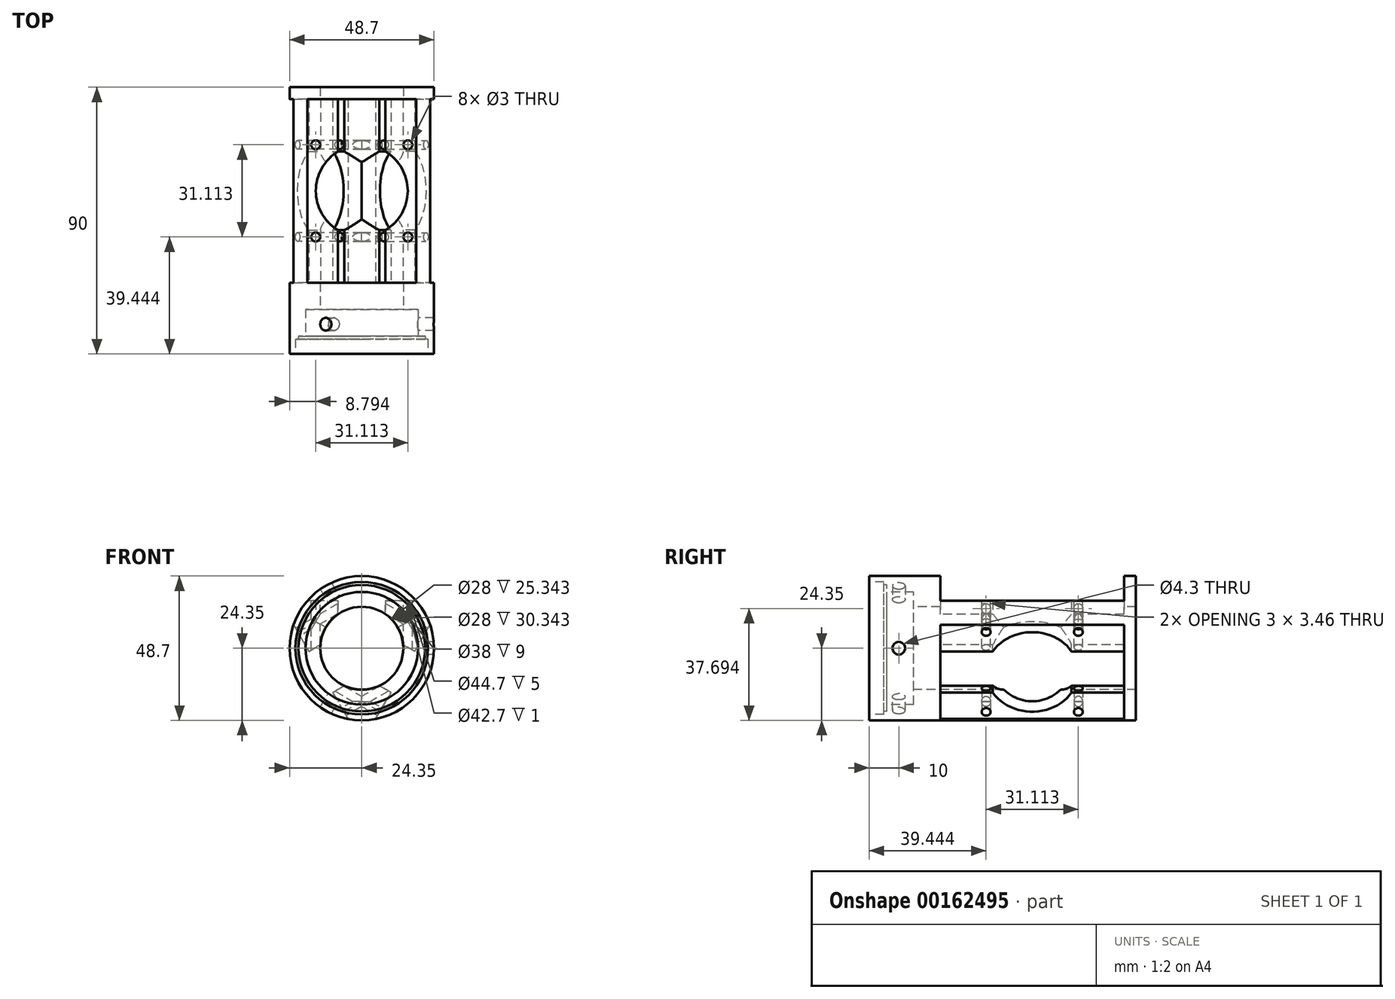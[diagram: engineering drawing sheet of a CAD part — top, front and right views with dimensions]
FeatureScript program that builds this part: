
annotation { "Feature Type Name" : "Feature", "Feature Type Description" : "" }
export const myFeature = defineFeature(function(context is Context, id is Id, definition is map)
    precondition{}
    {
        {
            var Q0;
            Q0=qCreatedBy(makeId("Top.planeOp"),FACE);
            var sketch = newSketch(context, id + "F0", { "sketchPlane" : qUnion([Q0])});
            skLineSegment(sketch, "E0", {"start": v(22.35, 0) * mm, "end": v(22.35, 5) * mm});
            skLineSegment(sketch, "E1", {"start": v(22.35, 0) * mm, "end": v(24.35, 0) * mm});
            skLineSegment(sketch, "E2", {"start": v(24.35, 0) * mm, "end": v(24.35, 90) * mm});
            skLineSegment(sketch, "E3", {"start": v(24.35, 90) * mm, "end": v(14, 90) * mm});
            skLineSegment(sketch, "E4", {"start": v(22.35, 5) * mm, "end": v(21.35, 5) * mm});
            skLineSegment(sketch, "E5", {"start": v(21.35, 5) * mm, "end": v(21.35, 6) * mm});
            skLineSegment(sketch, "E6", {"start": v(21.35, 6) * mm, "end": v(19, 6) * mm});
            skLineSegment(sketch, "E7", {"start": v(14, 90) * mm, "end": v(14, 15) * mm});
            skLineSegment(sketch, "E8", {"start": v(0, 0) * mm, "end": v(0, 47.68) * mm, "construction": true});
            skLineSegment(sketch, "E9", {"start": v(14, 15) * mm, "end": v(19, 15) * mm});
            skLineSegment(sketch, "E10", {"start": v(19, 15) * mm, "end": v(19, 6) * mm});
            skSolve(sketch);
        }
        {
            var Q0;
            Q0 = qSketchRegion(id + "F0", true);
            var Q1;
            Q1=sQuery(id+"F0.wireOp",EDGE,"E8");
            revolve(context, id + "F1", {"entities" : qUnion([Q0]), "axis" : qUnion([Q1]), "revolveType" : RevolveType.FULL});
        }
        {
            var Q0;
            Q0=qCreatedBy(makeId("Top.planeOp"),FACE);
            cPlane(context, id + "F2", {"entities" : qUnion([Q0]), "cplaneType" : CPlaneType.OFFSET, "offset" : 25 * mm, "width" : 150 * mm, "height" : 150 * mm});
        }
        {
            var Q0;
            Q0=makeQuery(id+"F1.opRevolve","SWEPT_FACE",FACE,{"disambiguationData":[OSD([sQuery(id+"F0.wireOp",EDGE,"E3")])]});
            cPlane(context, id + "F3", {"entities" : qUnion([Q0]), "cplaneType" : CPlaneType.OFFSET, "offset" : 35 * mm, "oppositeDirection" : true, "width" : 150 * mm, "height" : 150 * mm});
        }
        {
            var Q0;
            Q0=qCreatedBy(id+"F3.planeOp",FACE);
            var sketch = newSketch(context, id + "F4", { "sketchPlane" : qUnion([Q0])});
            skLineSegment(sketch, "E11.bottom", {"start": v(-30, 36) * mm, "end": v(30, 36) * mm});
            skLineSegment(sketch, "E11.top", {"start": v(-30, 16) * mm, "end": v(-8, 16) * mm});
            skLineSegment(sketch, "E11.left", {"start": v(-30, 36) * mm, "end": v(-30, 16) * mm});
            skLineSegment(sketch, "E11.right", {"start": v(30, 36) * mm, "end": v(30, 16) * mm});
            skLineSegment(sketch, "E12", {"start": v(0, 0) * mm, "end": v(0, 8.26) * mm, "construction": true});
            skLineSegment(sketch, "E13", {"start": v(-8, 16) * mm, "end": v(-8, 0) * mm});
            skLineSegment(sketch, "E14.MirrorCS", {"start": v(8, 16) * mm, "end": v(8, 0) * mm});
            skLineSegment(sketch, "E15", {"start": v(-8, 0) * mm, "end": v(8, 0) * mm});
            skLineSegment(sketch, "E16.trimOffspring", {"start": v(8, 16) * mm, "end": v(30, 16) * mm});
            skSolve(sketch);
        }
        {
            var Q0;
            Q0 = qSketchRegion(id + "F4", true);
            extrude(context, id + "F5", {"entities" : qUnion([Q0]), "endBound" : BoundingType.SYMMETRIC, "depth" : 62 * mm});
        }
        {
            var Q0;
            Q0=makeQuery(id+"F5.opExtrude","SWEPT_BODY",BODY,{"disambiguationData":[OSD([sQuery(id+"F4.wireOp",EDGE,"E11.bottom"),sQuery(id+"F4.wireOp",EDGE,"E11.top"),sQuery(id+"F4.wireOp",EDGE,"E11.left"),sQuery(id+"F4.wireOp",EDGE,"E11.right")])]});
            var Q1;
            Q1=makeQuery(id+"F1.opRevolve","SWEPT_FACE",FACE,{"disambiguationData":[OSD([sQuery(id+"F0.wireOp",EDGE,"E7")])]});
            circularPattern(context, id + "F6", {"entities" : qUnion([Q0]), "axis" : qUnion([Q1]), "angle" : 120 * degree, "instanceCount" : 3});
        }
        {
            var Q0;
            Q0=makeQuery(id+"F5.opExtrude","SWEPT_BODY",BODY,{"disambiguationData":[OSD([sQuery(id+"F4.wireOp",EDGE,"E11.bottom"),sQuery(id+"F4.wireOp",EDGE,"E11.top"),sQuery(id+"F4.wireOp",EDGE,"E11.left"),sQuery(id+"F4.wireOp",EDGE,"E11.right")])]});
            var Q1;
            Q1=makeQuery(id+"F6.opPattern","COPY",BODY,{"derivedFrom":makeQuery(id+"F5.opExtrude","SWEPT_BODY",BODY,{"disambiguationData":[OSD([sQuery(id+"F4.wireOp",EDGE,"E11.bottom"),sQuery(id+"F4.wireOp",EDGE,"E11.top"),sQuery(id+"F4.wireOp",EDGE,"E11.left"),sQuery(id+"F4.wireOp",EDGE,"E11.right")])]}),"instanceName":"2"});
            var Q2;
            Q2=makeQuery(id+"F6.opPattern","COPY",BODY,{"derivedFrom":makeQuery(id+"F5.opExtrude","SWEPT_BODY",BODY,{"disambiguationData":[OSD([sQuery(id+"F4.wireOp",EDGE,"E11.bottom"),sQuery(id+"F4.wireOp",EDGE,"E11.top"),sQuery(id+"F4.wireOp",EDGE,"E11.left"),sQuery(id+"F4.wireOp",EDGE,"E11.right")])]}),"instanceName":"1"});
            var Q3;
            Q3=makeQuery(id+"F1.opRevolve","SWEPT_BODY",BODY,{"disambiguationData":[OSD([sQuery(id+"F0.wireOp",EDGE,"E0"),sQuery(id+"F0.wireOp",EDGE,"E1"),sQuery(id+"F0.wireOp",EDGE,"E2"),sQuery(id+"F0.wireOp",EDGE,"E3"),sQuery(id+"F0.wireOp",EDGE,"E4"),sQuery(id+"F0.wireOp",EDGE,"E5"),sQuery(id+"F0.wireOp",EDGE,"E6"),sQuery(id+"F0.wireOp",EDGE,"E7")])]});
            booleanBodies(context, id + "F7", {"operationType" : BooleanOperationType.SUBTRACTION, "tools" : qUnion([Q0, Q1, Q2]), "targets" : qUnion([Q3])});
        }
        {
            var Q0;
            Q0=qCreatedBy(id+"F2.planeOp",FACE);
            var sketch = newSketch(context, id + "F8", { "sketchPlane" : qUnion([Q0])});
            skCircle(sketch, "E17", {"center": v(0, 55) * mm, "radius": 22 * mm, "construction": true});
            skLineSegment(sketch, "E18", {"start": v(0, 55) * mm, "end": v(18.83, 73.83) * mm, "construction": true});
            skCircle(sketch, "E19", {"center": v(15.56, 70.56) * mm, "radius": 1.5 * mm});
            skLineSegment(sketch, "E20", {"start": v(0, 55) * mm, "end": v(-13.28, 68.28) * mm, "construction": true});
            skCircle(sketch, "E21.MirrorC", {"center": v(-15.56, 39.44) * mm, "radius": 1.5 * mm});
            skLineSegment(sketch, "E22", {"start": v(0, 55) * mm, "end": v(-17.58, 55) * mm, "construction": true});
            skCircle(sketch, "E23.MirrorC", {"center": v(-15.56, 70.56) * mm, "radius": 1.5 * mm});
            skCircle(sketch, "E24.MirrorC", {"center": v(15.56, 39.44) * mm, "radius": 1.5 * mm});
            skSolve(sketch);
        }
        {
            var Q0;
            Q0 = qSketchRegion(id + "F8", true);
            extrude(context, id + "F9", {"entities" : qUnion([Q0]), "endBound" : BoundingType.THROUGH_ALL, "oppositeDirection" : true, "depth" : 25 * mm});
        }
        {
            var Q0;
            Q0=makeQuery(id+"F9.opExtrude","SWEPT_BODY",BODY,{"disambiguationData":[OSD([sQuery(id+"F8.wireOp",EDGE,"E19")])]});
            var Q1;
            Q1=makeQuery(id+"F9.opExtrude","SWEPT_BODY",BODY,{"disambiguationData":[OSD([sQuery(id+"F8.wireOp",EDGE,"E21.MirrorC")])]});
            var Q2;
            Q2=makeQuery(id+"F9.opExtrude","SWEPT_BODY",BODY,{"disambiguationData":[OSD([sQuery(id+"F8.wireOp",EDGE,"E24.MirrorC")])]});
            var Q3;
            Q3=makeQuery(id+"F9.opExtrude","SWEPT_BODY",BODY,{"disambiguationData":[OSD([sQuery(id+"F8.wireOp",EDGE,"E23.MirrorC")])]});
            var Q4;
            Q4=makeQuery(id+"F7.opBoolean","SPLIT",FACE,{"disambiguationData":[TD([makeQuery(id+"F1.opRevolve","SWEPT_FACE",FACE,{"disambiguationData":[OSD([sQuery(id+"F0.wireOp",EDGE,"E6")])]})])],"derivedFrom":makeQuery(id+"F1.opRevolve","SWEPT_FACE",FACE,{"disambiguationData":[OSD([sQuery(id+"F0.wireOp",EDGE,"E7")])]})});
            circularPattern(context, id + "F10", {"entities" : qUnion([Q0, Q1, Q2, Q3]), "axis" : qUnion([Q4]), "angle" : 120 * degree, "instanceCount" : 3});
        }
        {
            var Q0;
            Q0=makeQuery(id+"F9.opExtrude","SWEPT_BODY",BODY,{"disambiguationData":[OSD([sQuery(id+"F8.wireOp",EDGE,"E19")])]});
            var Q1;
            Q1=makeQuery(id+"F10.opPattern","COPY",BODY,{"derivedFrom":makeQuery(id+"F9.opExtrude","SWEPT_BODY",BODY,{"disambiguationData":[OSD([sQuery(id+"F8.wireOp",EDGE,"E21.MirrorC")])]}),"instanceName":"2"});
            var Q2;
            Q2=makeQuery(id+"F10.opPattern","COPY",BODY,{"derivedFrom":makeQuery(id+"F9.opExtrude","SWEPT_BODY",BODY,{"disambiguationData":[OSD([sQuery(id+"F8.wireOp",EDGE,"E21.MirrorC")])]}),"instanceName":"1"});
            var Q3;
            Q3=makeQuery(id+"F10.opPattern","COPY",BODY,{"derivedFrom":makeQuery(id+"F9.opExtrude","SWEPT_BODY",BODY,{"disambiguationData":[OSD([sQuery(id+"F8.wireOp",EDGE,"E19")])]}),"instanceName":"2"});
            var Q4;
            Q4=makeQuery(id+"F9.opExtrude","SWEPT_BODY",BODY,{"disambiguationData":[OSD([sQuery(id+"F8.wireOp",EDGE,"E21.MirrorC")])]});
            var Q5;
            Q5=makeQuery(id+"F10.opPattern","COPY",BODY,{"derivedFrom":makeQuery(id+"F9.opExtrude","SWEPT_BODY",BODY,{"disambiguationData":[OSD([sQuery(id+"F8.wireOp",EDGE,"E19")])]}),"instanceName":"1"});
            var Q6;
            Q6=makeQuery(id+"F9.opExtrude","SWEPT_BODY",BODY,{"disambiguationData":[OSD([sQuery(id+"F8.wireOp",EDGE,"E24.MirrorC")])]});
            var Q7;
            Q7=makeQuery(id+"F10.opPattern","COPY",BODY,{"derivedFrom":makeQuery(id+"F9.opExtrude","SWEPT_BODY",BODY,{"disambiguationData":[OSD([sQuery(id+"F8.wireOp",EDGE,"E24.MirrorC")])]}),"instanceName":"2"});
            var Q8;
            Q8=makeQuery(id+"F10.opPattern","COPY",BODY,{"derivedFrom":makeQuery(id+"F9.opExtrude","SWEPT_BODY",BODY,{"disambiguationData":[OSD([sQuery(id+"F8.wireOp",EDGE,"E23.MirrorC")])]}),"instanceName":"1"});
            var Q9;
            Q9=makeQuery(id+"F9.opExtrude","SWEPT_BODY",BODY,{"disambiguationData":[OSD([sQuery(id+"F8.wireOp",EDGE,"E23.MirrorC")])]});
            var Q10;
            Q10=makeQuery(id+"F10.opPattern","COPY",BODY,{"derivedFrom":makeQuery(id+"F9.opExtrude","SWEPT_BODY",BODY,{"disambiguationData":[OSD([sQuery(id+"F8.wireOp",EDGE,"E23.MirrorC")])]}),"instanceName":"2"});
            var Q11;
            Q11=makeQuery(id+"F10.opPattern","COPY",BODY,{"derivedFrom":makeQuery(id+"F9.opExtrude","SWEPT_BODY",BODY,{"disambiguationData":[OSD([sQuery(id+"F8.wireOp",EDGE,"E24.MirrorC")])]}),"instanceName":"1"});
            var Q12;
            Q12=makeQuery(id+"F1.opRevolve","SWEPT_BODY",BODY,{"disambiguationData":[OSD([sQuery(id+"F0.wireOp",EDGE,"E0"),sQuery(id+"F0.wireOp",EDGE,"E1"),sQuery(id+"F0.wireOp",EDGE,"E2"),sQuery(id+"F0.wireOp",EDGE,"E3"),sQuery(id+"F0.wireOp",EDGE,"E4"),sQuery(id+"F0.wireOp",EDGE,"E5"),sQuery(id+"F0.wireOp",EDGE,"E6"),sQuery(id+"F0.wireOp",EDGE,"E7")])]});
            booleanBodies(context, id + "F11", {"operationType" : BooleanOperationType.SUBTRACTION, "tools" : qUnion([Q0, Q1, Q2, Q3, Q4, Q5, Q6, Q7, Q8, Q9, Q10, Q11]), "targets" : qUnion([Q12])});
        }
        {
            var Q0;
            Q0=qCreatedBy(makeId("Right.planeOp"),FACE);
            var sketch = newSketch(context, id + "F12", { "sketchPlane" : qUnion([Q0])});
            skCircle(sketch, "E25", {"center": v(10, 0) * mm, "radius": 2.15 * mm});
            skSolve(sketch);
        }
        {
            var Q0;
            Q0 = qSketchRegion(id + "F12", true);
            extrude(context, id + "F13", {"entities" : qUnion([Q0]), "depth" : 50 * mm, "hasSecondDirection" : true, "secondDirectionOppositeDirection" : false, "secondDirectionDepth" : 5 * mm});
        }
        {
            var Q0;
            Q0=makeQuery(id+"F13.opExtrude","SWEPT_BODY",BODY,{"disambiguationData":[OSD([sQuery(id+"F12.wireOp",EDGE,"E25")])]});
            var Q1;
            Q1=makeQuery(id+"F1.opRevolve","SWEPT_FACE",FACE,{"disambiguationData":[OSD([sQuery(id+"F0.wireOp",EDGE,"E7")])]});
            circularPattern(context, id + "F14", {"entities" : qUnion([Q0]), "axis" : qUnion([Q1]), "angle" : 120 * degree, "instanceCount" : 3});
        }
        {
            var Q0;
            Q0=makeQuery(id+"F14.opPattern","COPY",BODY,{"derivedFrom":makeQuery(id+"F13.opExtrude","SWEPT_BODY",BODY,{"disambiguationData":[OSD([sQuery(id+"F12.wireOp",EDGE,"E25")])]}),"instanceName":"1"});
            var Q1;
            Q1=makeQuery(id+"F14.opPattern","COPY",BODY,{"derivedFrom":makeQuery(id+"F13.opExtrude","SWEPT_BODY",BODY,{"disambiguationData":[OSD([sQuery(id+"F12.wireOp",EDGE,"E25")])]}),"instanceName":"2"});
            var Q2;
            Q2=makeQuery(id+"F13.opExtrude","SWEPT_BODY",BODY,{"disambiguationData":[OSD([sQuery(id+"F12.wireOp",EDGE,"E25")])]});
            var Q3;
            Q3=makeQuery(id+"F1.opRevolve","SWEPT_BODY",BODY,{"disambiguationData":[OSD([sQuery(id+"F0.wireOp",EDGE,"E0"),sQuery(id+"F0.wireOp",EDGE,"E1"),sQuery(id+"F0.wireOp",EDGE,"E2"),sQuery(id+"F0.wireOp",EDGE,"E3"),sQuery(id+"F0.wireOp",EDGE,"E4"),sQuery(id+"F0.wireOp",EDGE,"E5"),sQuery(id+"F0.wireOp",EDGE,"E6"),sQuery(id+"F0.wireOp",EDGE,"E7")])]});
            booleanBodies(context, id + "F15", {"operationType" : BooleanOperationType.SUBTRACTION, "tools" : qUnion([Q0, Q1, Q2]), "targets" : qUnion([Q3])});
        }
        {
            var Q0;
            Q0=makeQuery(id+"F7.opBoolean","COPY",FACE,{"derivedFrom":makeQuery(id+"F5.opExtrude","SWEPT_FACE",FACE,{"disambiguationData":[OSD([sQuery(id+"F4.wireOp",EDGE,"E11.top")])]})});
            var sketch = newSketch(context, id + "F16", { "sketchPlane" : qUnion([Q0])});
            skCircle(sketch, "E26", {"center": v(0, 55) * mm, "radius": 15.5 * mm});
            skPoint(sketch, "E26.centerSnap0", {"position": v(8, 55) * mm});
            skSolve(sketch);
        }
        {
            var Q0;
            Q0 = qSketchRegion(id + "F16", true);
            extrude(context, id + "F17", {"entities" : qUnion([Q0]), "endBound" : BoundingType.SYMMETRIC, "depth" : 40 * mm});
        }
        {
            var Q0;
            Q0=makeQuery(id+"F17.opExtrude","SWEPT_BODY",BODY,{"disambiguationData":[OSD([sQuery(id+"F16.wireOp",EDGE,"E26")])]});
            var Q1;
            Q1=makeQuery(id+"F1.opRevolve","SWEPT_FACE",FACE,{"disambiguationData":[OSD([sQuery(id+"F0.wireOp",EDGE,"E7")])]});
            circularPattern(context, id + "F18", {"entities" : qUnion([Q0]), "axis" : qUnion([Q1]), "angle" : 120 * degree, "instanceCount" : 3});
        }
        {
            var Q0;
            Q0=makeQuery(id+"F18.opPattern","COPY",BODY,{"derivedFrom":makeQuery(id+"F17.opExtrude","SWEPT_BODY",BODY,{"disambiguationData":[OSD([sQuery(id+"F16.wireOp",EDGE,"E26")])]}),"instanceName":"2"});
            var Q1;
            Q1=makeQuery(id+"F17.opExtrude","SWEPT_BODY",BODY,{"disambiguationData":[OSD([sQuery(id+"F16.wireOp",EDGE,"E26")])]});
            var Q2;
            Q2=makeQuery(id+"F18.opPattern","COPY",BODY,{"derivedFrom":makeQuery(id+"F17.opExtrude","SWEPT_BODY",BODY,{"disambiguationData":[OSD([sQuery(id+"F16.wireOp",EDGE,"E26")])]}),"instanceName":"1"});
            var Q3;
            Q3=makeQuery(id+"F1.opRevolve","SWEPT_BODY",BODY,{"disambiguationData":[OSD([sQuery(id+"F0.wireOp",EDGE,"E0"),sQuery(id+"F0.wireOp",EDGE,"E1"),sQuery(id+"F0.wireOp",EDGE,"E2"),sQuery(id+"F0.wireOp",EDGE,"E3"),sQuery(id+"F0.wireOp",EDGE,"E4"),sQuery(id+"F0.wireOp",EDGE,"E5"),sQuery(id+"F0.wireOp",EDGE,"E6"),sQuery(id+"F0.wireOp",EDGE,"E7"),sQuery(id+"F0.wireOp",EDGE,"E9"),sQuery(id+"F0.wireOp",EDGE,"E10")])]});
            booleanBodies(context, id + "F19", {"operationType" : BooleanOperationType.SUBTRACTION, "tools" : qUnion([Q0, Q1, Q2]), "targets" : qUnion([Q3])});
        }
    });
